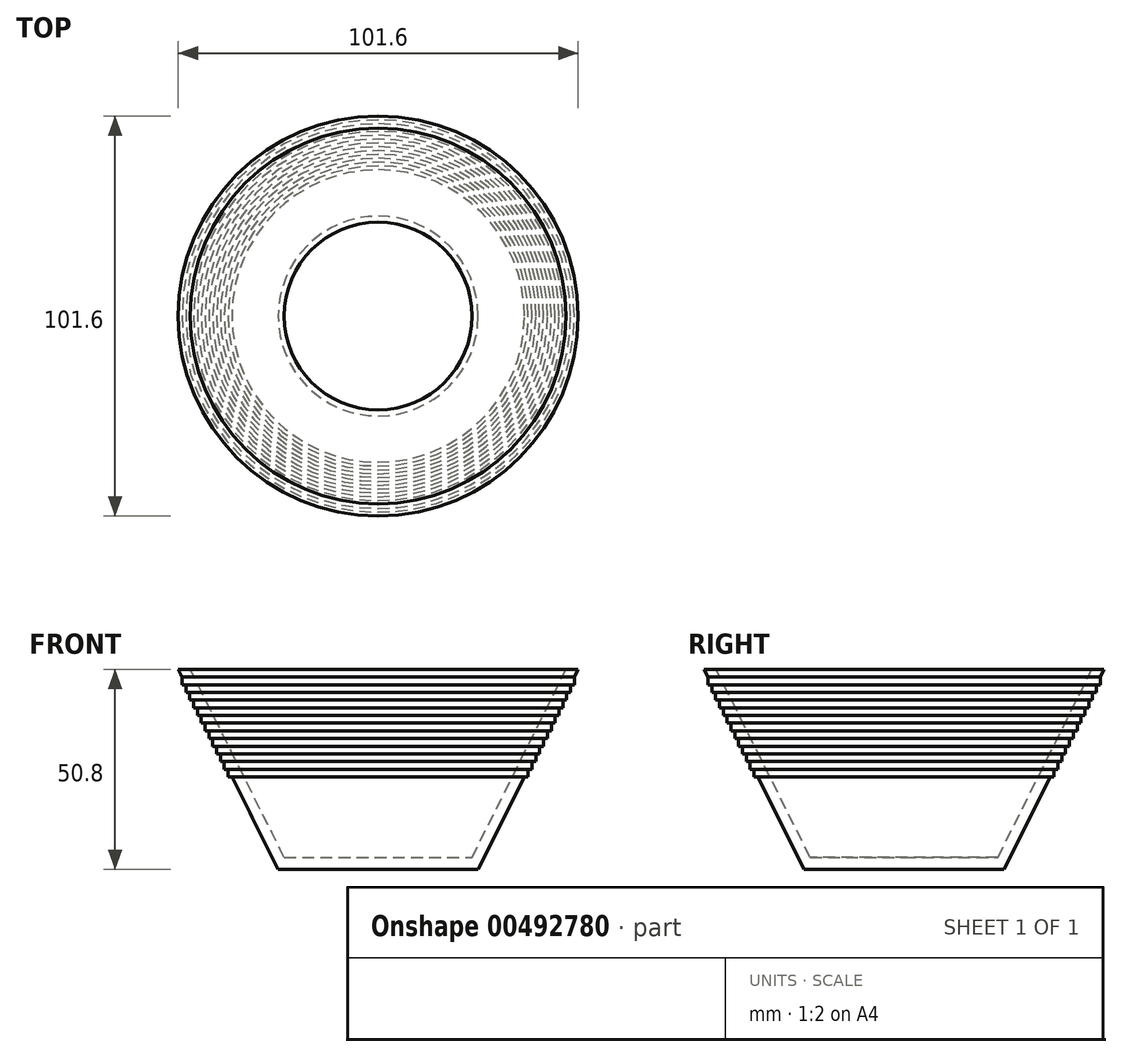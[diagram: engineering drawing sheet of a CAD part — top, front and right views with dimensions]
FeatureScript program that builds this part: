
annotation { "Feature Type Name" : "Feature", "Feature Type Description" : "" }
export const myFeature = defineFeature(function(context is Context, id is Id, definition is map)
    precondition{}
    {
        {
            var Q0;
            Q0=qCreatedBy(makeId("Front.planeOp"),FACE);
            var sketch = newSketch(context, id + "F0", { "sketchPlane" : qUnion([Q0])});
            skLineSegment(sketch, "E0", {"start": v(0, 0) * mm, "end": v(25.4, 0) * mm});
            skLineSegment(sketch, "E1", {"start": v(25.4, 0) * mm, "end": v(50.8, 50.8) * mm});
            skLineSegment(sketch, "E2", {"start": v(0, 0) * mm, "end": v(0, 50.8) * mm, "construction": true});
            skLineSegment(sketch, "E3", {"start": v(0, 3.07) * mm, "end": v(23.86, 3.07) * mm});
            skLineSegment(sketch, "E4", {"start": v(23.86, 3.07) * mm, "end": v(47.73, 50.8) * mm});
            skLineSegment(sketch, "E5", {"start": v(47.73, 50.8) * mm, "end": v(50.8, 50.8) * mm});
            skLineSegment(sketch, "E6", {"start": v(0, 3.07) * mm, "end": v(0, 0) * mm});
            skLineSegment(sketch, "E7", {"start": v(49.83, 48.87) * mm, "end": v(49.83, 46.91) * mm});
            skLineSegment(sketch, "E8", {"start": v(49.83, 46.91) * mm, "end": v(48.86, 46.91) * mm});
            skLineSegment(sketch, "E9", {"start": v(48.86, 46.91) * mm, "end": v(48.86, 44.96) * mm});
            skLineSegment(sketch, "E10", {"start": v(48.86, 44.96) * mm, "end": v(47.88, 44.96) * mm});
            skLineSegment(sketch, "E11", {"start": v(47.88, 44.96) * mm, "end": v(47.88, 43) * mm});
            skLineSegment(sketch, "E12", {"start": v(47.88, 43) * mm, "end": v(46.9, 43) * mm});
            skLineSegment(sketch, "E13", {"start": v(46.9, 43) * mm, "end": v(46.9, 41.06) * mm});
            skLineSegment(sketch, "E14", {"start": v(46.9, 41.06) * mm, "end": v(45.93, 41.06) * mm});
            skLineSegment(sketch, "E15", {"start": v(45.93, 41.06) * mm, "end": v(45.93, 39.1) * mm});
            skLineSegment(sketch, "E16", {"start": v(45.93, 39.1) * mm, "end": v(44.95, 39.1) * mm});
            skLineSegment(sketch, "E17", {"start": v(44.95, 39.1) * mm, "end": v(44.95, 37.16) * mm});
            skLineSegment(sketch, "E18", {"start": v(44.95, 37.16) * mm, "end": v(43.98, 37.16) * mm});
            skLineSegment(sketch, "E19", {"start": v(43.98, 37.16) * mm, "end": v(43.98, 35.2) * mm});
            skLineSegment(sketch, "E20", {"start": v(43.98, 35.2) * mm, "end": v(43, 35.2) * mm});
            skLineSegment(sketch, "E21", {"start": v(43, 35.2) * mm, "end": v(43, 33.25) * mm});
            skLineSegment(sketch, "E22", {"start": v(43, 33.25) * mm, "end": v(42.02, 33.25) * mm});
            skLineSegment(sketch, "E23", {"start": v(42.02, 33.25) * mm, "end": v(42.02, 31.3) * mm});
            skLineSegment(sketch, "E24", {"start": v(42.02, 31.3) * mm, "end": v(41.05, 31.3) * mm});
            skLineSegment(sketch, "E25", {"start": v(41.05, 31.3) * mm, "end": v(41.05, 29.35) * mm});
            skLineSegment(sketch, "E26", {"start": v(41.05, 29.35) * mm, "end": v(40.07, 29.35) * mm});
            skLineSegment(sketch, "E27", {"start": v(40.07, 29.35) * mm, "end": v(40.07, 27.4) * mm});
            skLineSegment(sketch, "E28", {"start": v(40.07, 27.4) * mm, "end": v(39.1, 27.4) * mm});
            skLineSegment(sketch, "E29", {"start": v(39.1, 27.4) * mm, "end": v(39.1, 25.44) * mm});
            skLineSegment(sketch, "E30", {"start": v(39.1, 25.44) * mm, "end": v(38.12, 25.44) * mm});
            skLineSegment(sketch, "E31", {"start": v(38.12, 25.44) * mm, "end": v(38.12, 23.5) * mm});
            skLineSegment(sketch, "E32", {"start": v(38.12, 23.5) * mm, "end": v(37.15, 23.5) * mm});
            skLineSegment(sketch, "E33", {"start": v(49.83, 48.87) * mm, "end": v(37.15, 23.5) * mm});
            skSolve(sketch);
        }
        {
            var Q0;
            {var subQ0=sQuery(id+"F0.wireOp",EDGE,"E11");Q0=makeQuery(id+"F0.imprint","IMPRINT",FACE,{"disambiguationData":[TD([[makeQuery(id+"F0.imprint","IMPRINT",EDGE,{"derivedFrom":subQ0}),-1.0]])]});}
            var Q1;
            {var subQ0=sQuery(id+"F0.wireOp",EDGE,"E9");Q1=makeQuery(id+"F0.imprint","IMPRINT",FACE,{"disambiguationData":[TD([[makeQuery(id+"F0.imprint","IMPRINT",EDGE,{"derivedFrom":subQ0}),-1.0]])]});}
            var Q2;
            {var subQ0=sQuery(id+"F0.wireOp",EDGE,"E7");Q2=makeQuery(id+"F0.imprint","IMPRINT",FACE,{"disambiguationData":[TD([[makeQuery(id+"F0.imprint","IMPRINT",EDGE,{"derivedFrom":subQ0}),-1.0]])]});}
            var Q3;
            {var subQ0=sQuery(id+"F0.wireOp",EDGE,"E13");Q3=makeQuery(id+"F0.imprint","IMPRINT",FACE,{"disambiguationData":[TD([[makeQuery(id+"F0.imprint","IMPRINT",EDGE,{"derivedFrom":subQ0}),-1.0]])]});}
            var Q4;
            {var subQ0=sQuery(id+"F0.wireOp",EDGE,"E15");Q4=makeQuery(id+"F0.imprint","IMPRINT",FACE,{"disambiguationData":[TD([[makeQuery(id+"F0.imprint","IMPRINT",EDGE,{"derivedFrom":subQ0}),-1.0]])]});}
            var Q5;
            {var subQ0=sQuery(id+"F0.wireOp",EDGE,"E17");Q5=makeQuery(id+"F0.imprint","IMPRINT",FACE,{"disambiguationData":[TD([[makeQuery(id+"F0.imprint","IMPRINT",EDGE,{"derivedFrom":subQ0}),-1.0]])]});}
            var Q6;
            {var subQ0=sQuery(id+"F0.wireOp",EDGE,"E19");Q6=makeQuery(id+"F0.imprint","IMPRINT",FACE,{"disambiguationData":[TD([[makeQuery(id+"F0.imprint","IMPRINT",EDGE,{"derivedFrom":subQ0}),-1.0]])]});}
            var Q7;
            {var subQ0=sQuery(id+"F0.wireOp",EDGE,"E21");Q7=makeQuery(id+"F0.imprint","IMPRINT",FACE,{"disambiguationData":[TD([[makeQuery(id+"F0.imprint","IMPRINT",EDGE,{"derivedFrom":subQ0}),-1.0]])]});}
            var Q8;
            {var subQ0=sQuery(id+"F0.wireOp",EDGE,"E23");Q8=makeQuery(id+"F0.imprint","IMPRINT",FACE,{"disambiguationData":[TD([[makeQuery(id+"F0.imprint","IMPRINT",EDGE,{"derivedFrom":subQ0}),-1.0]])]});}
            var Q9;
            {var subQ0=sQuery(id+"F0.wireOp",EDGE,"E25");Q9=makeQuery(id+"F0.imprint","IMPRINT",FACE,{"disambiguationData":[TD([[makeQuery(id+"F0.imprint","IMPRINT",EDGE,{"derivedFrom":subQ0}),-1.0]])]});}
            var Q10;
            {var subQ0=sQuery(id+"F0.wireOp",EDGE,"E27");Q10=makeQuery(id+"F0.imprint","IMPRINT",FACE,{"disambiguationData":[TD([[makeQuery(id+"F0.imprint","IMPRINT",EDGE,{"derivedFrom":subQ0}),-1.0]])]});}
            var Q11;
            {var subQ0=sQuery(id+"F0.wireOp",EDGE,"E29");Q11=makeQuery(id+"F0.imprint","IMPRINT",FACE,{"disambiguationData":[TD([[makeQuery(id+"F0.imprint","IMPRINT",EDGE,{"derivedFrom":subQ0}),-1.0]])]});}
            var Q12;
            {var subQ0=sQuery(id+"F0.wireOp",EDGE,"E31");Q12=makeQuery(id+"F0.imprint","IMPRINT",FACE,{"disambiguationData":[TD([[makeQuery(id+"F0.imprint","IMPRINT",EDGE,{"derivedFrom":subQ0}),-1.0]])]});}
            var Q13;
            {var subQ5=sQuery(id+"F0.wireOp",EDGE,"E0");Q13=makeQuery(id+"F0.imprint","IMPRINT",FACE,{"disambiguationData":[TD([[makeQuery(id+"F0.imprint","IMPRINT",EDGE,{"derivedFrom":subQ5}),1.0]])]});}
            var Q14;
            Q14=sQuery(id+"F0.wireOp",EDGE,"E2");
            revolve(context, id + "F1", {"entities" : qUnion([Q0, Q1, Q2, Q3, Q4, Q5, Q6, Q7, Q8, Q9, Q10, Q11, Q12, Q13]), "axis" : qUnion([Q14]), "revolveType" : RevolveType.FULL});
        }
    });
